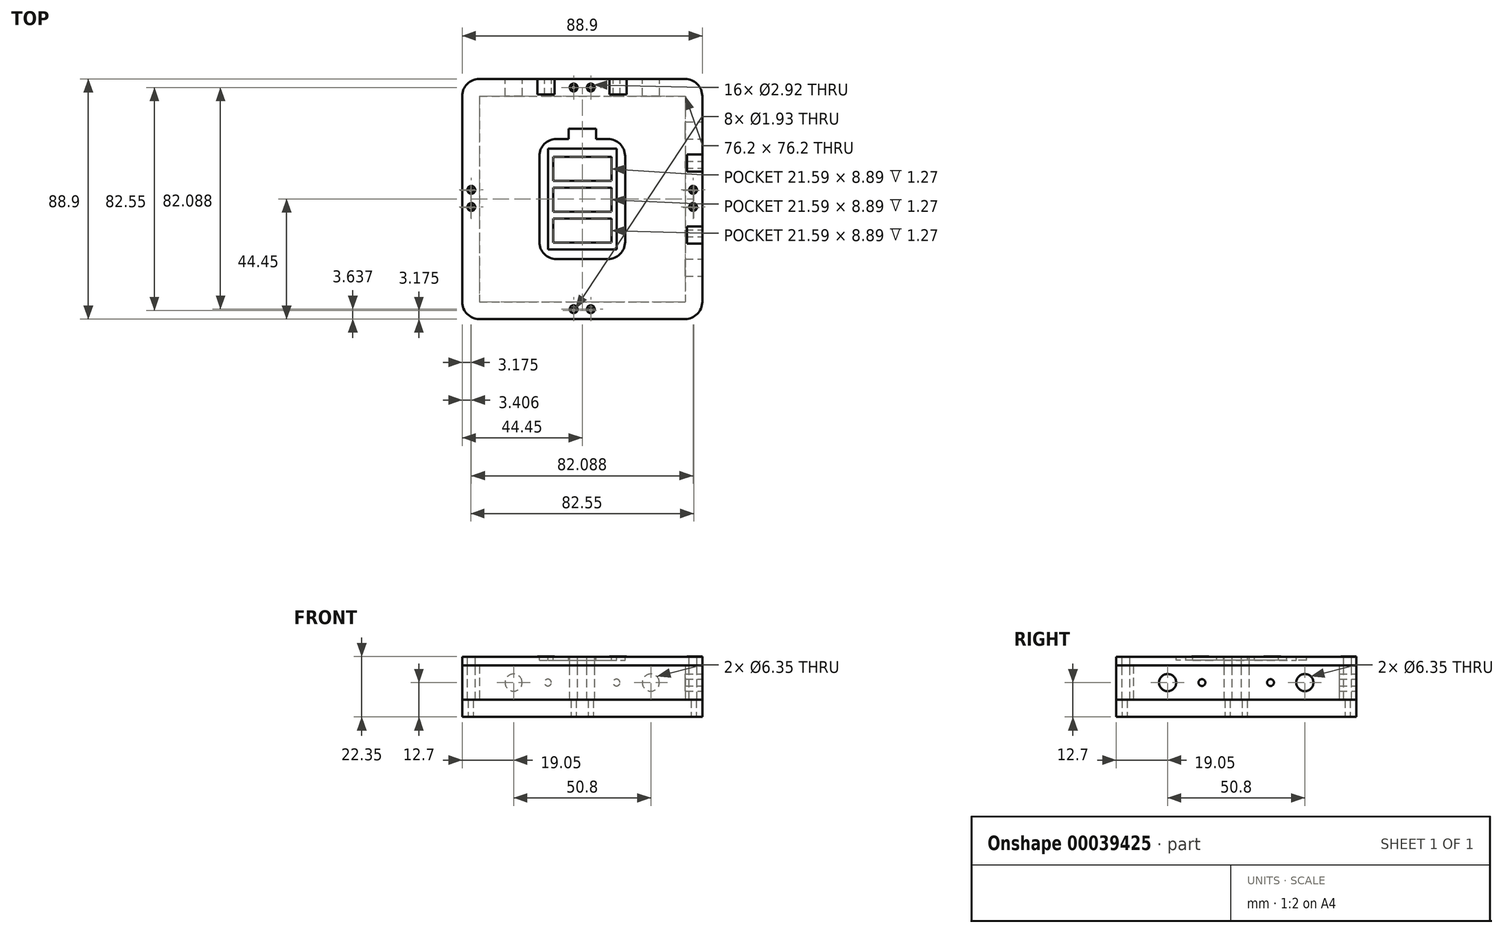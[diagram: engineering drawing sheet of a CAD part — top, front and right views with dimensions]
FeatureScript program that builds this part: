
annotation { "Feature Type Name" : "Feature", "Feature Type Description" : "" }
export const myFeature = defineFeature(function(context is Context, id is Id, definition is map)
    precondition{}
    {
        {
            var Q0;
            Q0=qCreatedBy(makeId("Top.planeOp"),FACE);
            var sketch = newSketch(context, id + "F0", { "sketchPlane" : qUnion([Q0])});
            skLineSegment(sketch, "E0.rect.bottom", {"start": v(-38.1, 44.45) * mm, "end": v(38.1, 44.45) * mm});
            skLineSegment(sketch, "E0.rect.top", {"start": v(-38.1, -44.45) * mm, "end": v(38.1, -44.45) * mm});
            skLineSegment(sketch, "E0.rect.left", {"start": v(-44.45, 38.1) * mm, "end": v(-44.45, -38.1) * mm});
            skLineSegment(sketch, "E0.rect.right", {"start": v(44.45, 38.1) * mm, "end": v(44.45, -38.1) * mm});
            skPoint(sketch, "E0.rect.middle", {"position": v(0, 0) * mm});
            skPoint(sketch, "E1.visualSharp", {"position": v(-44.45, 44.45) * mm});
            skArc(sketch, "E1.filletArc", {"start": v(-38.1, 44.45) * mm, "mid": v(-42.6, 42.6) * mm, "end": v(-44.45, 38.1) * mm});
            skPoint(sketch, "E2.visualSharp", {"position": v(44.45, 44.45) * mm});
            skArc(sketch, "E2.filletArc", {"start": v(44.45, 38.1) * mm, "mid": v(42.6, 42.6) * mm, "end": v(38.1, 44.45) * mm});
            skPoint(sketch, "E3.visualSharp", {"position": v(44.45, -44.45) * mm});
            skArc(sketch, "E3.filletArc", {"start": v(38.1, -44.45) * mm, "mid": v(42.6, -42.6) * mm, "end": v(44.45, -38.1) * mm});
            skPoint(sketch, "E4.visualSharp", {"position": v(-44.45, -44.45) * mm});
            skArc(sketch, "E4.filletArc", {"start": v(-44.45, -38.1) * mm, "mid": v(-42.6, -42.6) * mm, "end": v(-38.1, -44.45) * mm});
            skSolve(sketch);
        }
        {
            var Q0;
            Q0 = qSketchRegion(id + "F0", true);
            extrude(context, id + "F1", {"entities" : qUnion([Q0]), "depth" : 6.35 * mm});
        }
        {
            var Q0;
            Q0=makeQuery(id+"F1.opExtrude","CAP_FACE",FACE,{"disambiguationData":[OSD([sQuery(id+"F0.wireOp",EDGE,"E0.rect.bottom"),sQuery(id+"F0.wireOp",EDGE,"E0.rect.top"),sQuery(id+"F0.wireOp",EDGE,"E0.rect.left"),sQuery(id+"F0.wireOp",EDGE,"E0.rect.right"),sQuery(id+"F0.wireOp",EDGE,"E1.filletArc"),sQuery(id+"F0.wireOp",EDGE,"E2.filletArc"),sQuery(id+"F0.wireOp",EDGE,"E3.filletArc"),sQuery(id+"F0.wireOp",EDGE,"E4.filletArc")])],"isStart":false});
            var sketch = newSketch(context, id + "F2", { "sketchPlane" : qUnion([Q0])});
            skLineSegment(sketch, "E5.0", {"start": v(-38.1, 44.45) * mm, "end": v(38.1, 44.45) * mm});
            skArc(sketch, "E6.0", {"start": v(-38.1, 44.45) * mm, "mid": v(-42.6, 42.6) * mm, "end": v(-44.45, 38.1) * mm});
            skLineSegment(sketch, "E7.0", {"start": v(-44.45, 38.1) * mm, "end": v(-44.45, -38.1) * mm});
            skArc(sketch, "E8.0", {"start": v(-44.45, -38.1) * mm, "mid": v(-42.6, -42.6) * mm, "end": v(-38.1, -44.45) * mm});
            skLineSegment(sketch, "E9.0", {"start": v(-38.1, -44.45) * mm, "end": v(38.1, -44.45) * mm});
            skArc(sketch, "E10.0", {"start": v(38.1, -44.45) * mm, "mid": v(42.6, -42.6) * mm, "end": v(44.45, -38.1) * mm});
            skLineSegment(sketch, "E11.0", {"start": v(44.45, 38.1) * mm, "end": v(44.45, -38.1) * mm});
            skArc(sketch, "E12.0", {"start": v(44.45, 38.1) * mm, "mid": v(42.6, 42.6) * mm, "end": v(38.1, 44.45) * mm});
            skLineSegment(sketch, "E13.rect.bottom", {"start": v(-38.1, 38.1) * mm, "end": v(38.1, 38.1) * mm});
            skLineSegment(sketch, "E13.rect.top", {"start": v(-38.1, -38.1) * mm, "end": v(38.1, -38.1) * mm});
            skLineSegment(sketch, "E13.rect.left", {"start": v(-38.1, 38.1) * mm, "end": v(-38.1, -38.1) * mm});
            skLineSegment(sketch, "E13.rect.right", {"start": v(38.1, 38.1) * mm, "end": v(38.1, -38.1) * mm});
            skPoint(sketch, "E13.rect.middle", {"position": v(0, 0) * mm});
            skSolve(sketch);
        }
        {
            var Q0;
            Q0 = qSketchRegion(id + "F2", true);
            extrude(context, id + "F3", {"entities" : qUnion([Q0]), "depth" : 12.7 * mm});
        }
        {
            var Q0;
            Q0=makeQuery(id+"F3.opExtrude","SWEPT_FACE",FACE,{"disambiguationData":[OSD([sQuery(id+"F2.wireOp",EDGE,"E11.0")])]});
            var sketch = newSketch(context, id + "F4", { "sketchPlane" : qUnion([Q0])});
            skCircle(sketch, "E14", {"center": v(25.4, 12.7) * mm, "radius": 3.18 * mm});
            skPoint(sketch, "E14.centerSnap0", {"position": v(38.1, 12.7) * mm});
            skCircle(sketch, "E15", {"center": v(-25.4, 12.7) * mm, "radius": 3.18 * mm});
            skPoint(sketch, "E15.centerSnap0", {"position": v(-38.1, 12.7) * mm});
            skSolve(sketch);
        }
        {
            var Q0;
            Q0 = qSketchRegion(id + "F4", true);
            extrude(context, id + "F5", {"entities" : qUnion([Q0]), "operationType" : NewBodyOperationType.REMOVE, "oppositeDirection" : true, "depth" : 25.4 * mm});
        }
        {
            var Q0;
            Q0=makeQuery(id+"F3.opExtrude","SWEPT_FACE",FACE,{"disambiguationData":[OSD([sQuery(id+"F2.wireOp",EDGE,"E5.0")])]});
            var sketch = newSketch(context, id + "F6", { "sketchPlane" : qUnion([Q0])});
            skCircle(sketch, "E16", {"center": v(25.4, 12.7) * mm, "radius": 3.18 * mm});
            skPoint(sketch, "E16.centerSnap0", {"position": v(38.1, 12.7) * mm});
            skCircle(sketch, "E17", {"center": v(-25.4, 12.7) * mm, "radius": 3.18 * mm});
            skPoint(sketch, "E17.centerSnap0", {"position": v(-38.1, 12.7) * mm});
            skCircle(sketch, "E18", {"center": v(12.7, 12.7) * mm, "radius": 1.27 * mm});
            skCircle(sketch, "E19", {"center": v(-12.7, 12.7) * mm, "radius": 1.27 * mm});
            skSolve(sketch);
        }
        {
            var Q0;
            Q0 = qSketchRegion(id + "F6", true);
            extrude(context, id + "F7", {"entities" : qUnion([Q0]), "operationType" : NewBodyOperationType.REMOVE, "oppositeDirection" : true, "depth" : 25.4 * mm});
        }
        {
            var Q0;
            Q0=makeQuery(id+"F3.opExtrude","CAP_FACE",FACE,{"disambiguationData":[OSD([sQuery(id+"F2.wireOp",EDGE,"E5.0"),sQuery(id+"F2.wireOp",EDGE,"E6.0"),sQuery(id+"F2.wireOp",EDGE,"E7.0"),sQuery(id+"F2.wireOp",EDGE,"E8.0"),sQuery(id+"F2.wireOp",EDGE,"E9.0"),sQuery(id+"F2.wireOp",EDGE,"E10.0"),sQuery(id+"F2.wireOp",EDGE,"E11.0"),sQuery(id+"F2.wireOp",EDGE,"E12.0"),sQuery(id+"F2.wireOp",EDGE,"E13.rect.bottom"),sQuery(id+"F2.wireOp",EDGE,"E13.rect.top"),sQuery(id+"F2.wireOp",EDGE,"E13.rect.left"),sQuery(id+"F2.wireOp",EDGE,"E13.rect.right")])],"isStart":false});
            var sketch = newSketch(context, id + "F8", { "sketchPlane" : qUnion([Q0])});
            skArc(sketch, "E20.0", {"start": v(-38.1, 44.45) * mm, "mid": v(-42.6, 42.6) * mm, "end": v(-44.45, 38.1) * mm});
            skLineSegment(sketch, "E21.0", {"start": v(-38.1, 44.45) * mm, "end": v(38.1, 44.45) * mm});
            skArc(sketch, "E22.0", {"start": v(44.45, 38.1) * mm, "mid": v(42.6, 42.6) * mm, "end": v(38.1, 44.45) * mm});
            skLineSegment(sketch, "E23.0", {"start": v(44.45, 38.1) * mm, "end": v(44.45, -38.1) * mm});
            skArc(sketch, "E24.0", {"start": v(38.1, -44.45) * mm, "mid": v(42.6, -42.6) * mm, "end": v(44.45, -38.1) * mm});
            skLineSegment(sketch, "E25.0", {"start": v(-38.1, -44.45) * mm, "end": v(38.1, -44.45) * mm});
            skArc(sketch, "E26.0", {"start": v(-44.45, -38.1) * mm, "mid": v(-42.6, -42.6) * mm, "end": v(-38.1, -44.45) * mm});
            skLineSegment(sketch, "E27.0", {"start": v(-44.45, 38.1) * mm, "end": v(-44.45, -38.1) * mm});
            skSolve(sketch);
        }
        {
            var Q0;
            Q0 = qSketchRegion(id + "F8", true);
            extrude(context, id + "F9", {"entities" : qUnion([Q0]), "depth" : 3.17 * mm});
        }
        {
            var Q0;
            Q0=makeQuery(id+"F9.opExtrude","CAP_FACE",FACE,{"disambiguationData":[OSD([sQuery(id+"F8.wireOp",EDGE,"E20.0"),sQuery(id+"F8.wireOp",EDGE,"E21.0"),sQuery(id+"F8.wireOp",EDGE,"E22.0"),sQuery(id+"F8.wireOp",EDGE,"E23.0"),sQuery(id+"F8.wireOp",EDGE,"E24.0"),sQuery(id+"F8.wireOp",EDGE,"E25.0"),sQuery(id+"F8.wireOp",EDGE,"E26.0"),sQuery(id+"F8.wireOp",EDGE,"E27.0")])],"isStart":false});
            var sketch = newSketch(context, id + "F10", { "sketchPlane" : qUnion([Q0])});
            skCircle(sketch, "E28", {"center": v(-3.18, 41.28) * mm, "radius": 1.46 * mm});
            skCircle(sketch, "E29", {"center": v(3.17, 41.28) * mm, "radius": 1.46 * mm});
            skCircle(sketch, "E30.1.0", {"center": v(-41.04, -2.94) * mm, "radius": 1.46 * mm});
            skCircle(sketch, "E30.1.1", {"center": v(-41.04, 3.4) * mm, "radius": 1.46 * mm});
            skCircle(sketch, "E30.2.0", {"center": v(3.18, -40.81) * mm, "radius": 1.46 * mm});
            skCircle(sketch, "E30.2.1", {"center": v(-3.17, -40.81) * mm, "radius": 1.46 * mm});
            skCircle(sketch, "E30.3.0", {"center": v(41.04, 3.4) * mm, "radius": 1.46 * mm});
            skCircle(sketch, "E30.3.1", {"center": v(41.04, -2.94) * mm, "radius": 1.46 * mm});
            skPoint(sketch, "E30.center", {"position": v(0, 0.23) * mm});
            skSolve(sketch);
        }
        {
            var Q0;
            Q0 = qSketchRegion(id + "F10", true);
            extrude(context, id + "F11", {"entities" : qUnion([Q0]), "operationType" : NewBodyOperationType.REMOVE, "oppositeDirection" : true, "depth" : 15.88 * mm});
        }
        {
            var Q0;
            Q0=makeQuery(id+"F1.opExtrude","CAP_FACE",FACE,{"disambiguationData":[OSD([sQuery(id+"F0.wireOp",EDGE,"E0.rect.bottom"),sQuery(id+"F0.wireOp",EDGE,"E0.rect.top"),sQuery(id+"F0.wireOp",EDGE,"E0.rect.left"),sQuery(id+"F0.wireOp",EDGE,"E0.rect.right"),sQuery(id+"F0.wireOp",EDGE,"E1.filletArc"),sQuery(id+"F0.wireOp",EDGE,"E2.filletArc"),sQuery(id+"F0.wireOp",EDGE,"E3.filletArc"),sQuery(id+"F0.wireOp",EDGE,"E4.filletArc")])],"isStart":true});
            var sketch = newSketch(context, id + "F12", { "sketchPlane" : qUnion([Q0])});
            skCircle(sketch, "E31", {"center": v(3.18, -41.28) * mm, "radius": 0.97 * mm});
            skCircle(sketch, "E32", {"center": v(-3.17, -41.28) * mm, "radius": 0.97 * mm});
            skCircle(sketch, "E33.1.0", {"center": v(41.28, 3.18) * mm, "radius": 0.97 * mm});
            skCircle(sketch, "E33.1.1", {"center": v(41.28, -3.18) * mm, "radius": 0.97 * mm});
            skCircle(sketch, "E33.2.0", {"center": v(-3.17, 41.28) * mm, "radius": 0.97 * mm});
            skCircle(sketch, "E33.2.1", {"center": v(3.18, 41.28) * mm, "radius": 0.97 * mm});
            skCircle(sketch, "E33.3.0", {"center": v(-41.28, -3.17) * mm, "radius": 0.97 * mm});
            skCircle(sketch, "E33.3.1", {"center": v(-41.28, 3.18) * mm, "radius": 0.97 * mm});
            skPoint(sketch, "E33.center", {"position": v(0, 0) * mm});
            skSolve(sketch);
        }
        {
            var Q0;
            Q0 = qSketchRegion(id + "F12", true);
            extrude(context, id + "F13", {"entities" : qUnion([Q0]), "operationType" : NewBodyOperationType.REMOVE, "oppositeDirection" : true, "depth" : 6.35 * mm});
        }
        {
            var Q0;
            Q0=makeQuery(id+"F3.opExtrude","SWEPT_FACE",FACE,{"disambiguationData":[OSD([sQuery(id+"F2.wireOp",EDGE,"E11.0")])]});
            var sketch = newSketch(context, id + "F14", { "sketchPlane" : qUnion([Q0])});
            skCircle(sketch, "E34", {"center": v(-12.7, 12.7) * mm, "radius": 1.27 * mm});
            skPoint(sketch, "E34.centerSnap0", {"position": v(-38.1, 12.7) * mm});
            skCircle(sketch, "E35", {"center": v(12.7, 12.7) * mm, "radius": 1.27 * mm});
            skSolve(sketch);
        }
        {
            var Q0;
            Q0 = qSketchRegion(id + "F14", true);
            extrude(context, id + "F15", {"entities" : qUnion([Q0]), "operationType" : NewBodyOperationType.REMOVE, "oppositeDirection" : true, "depth" : 25.4 * mm});
        }
        {
            var Q0;
            Q0=makeQuery(id+"F9.opExtrude","CAP_FACE",FACE,{"disambiguationData":[OSD([sQuery(id+"F8.wireOp",EDGE,"E20.0"),sQuery(id+"F8.wireOp",EDGE,"E21.0"),sQuery(id+"F8.wireOp",EDGE,"E22.0"),sQuery(id+"F8.wireOp",EDGE,"E23.0"),sQuery(id+"F8.wireOp",EDGE,"E24.0"),sQuery(id+"F8.wireOp",EDGE,"E25.0"),sQuery(id+"F8.wireOp",EDGE,"E26.0"),sQuery(id+"F8.wireOp",EDGE,"E27.0")])],"isStart":false});
            var sketch = newSketch(context, id + "F16", { "sketchPlane" : qUnion([Q0])});
            skLineSegment(sketch, "E36.rect.bottom", {"start": v(-12.7, 18.64) * mm, "end": v(12.7, 18.64) * mm});
            skLineSegment(sketch, "E36.rect.top", {"start": v(-12.7, -18.64) * mm, "end": v(12.7, -18.64) * mm});
            skLineSegment(sketch, "E36.rect.left", {"start": v(-12.7, 18.64) * mm, "end": v(-12.7, -18.64) * mm});
            skLineSegment(sketch, "E36.rect.right", {"start": v(12.7, 18.64) * mm, "end": v(12.7, -18.64) * mm});
            skPoint(sketch, "E36.rect.middle", {"position": v(0, 0) * mm});
            skLineSegment(sketch, "E37.rect.bottom", {"start": v(-9.52, 22.25) * mm, "end": v(-5.08, 22.25) * mm});
            skLineSegment(sketch, "E37.rect.top", {"start": v(-9.53, -22.25) * mm, "end": v(9.52, -22.25) * mm});
            skLineSegment(sketch, "E37.rect.left", {"start": v(-15.87, 15.9) * mm, "end": v(-15.88, -15.9) * mm});
            skLineSegment(sketch, "E37.rect.right", {"start": v(15.88, 15.9) * mm, "end": v(15.87, -15.9) * mm});
            skPoint(sketch, "E38.visualSharp", {"position": v(-15.87, 22.25) * mm});
            skArc(sketch, "E38.filletArc", {"start": v(-9.52, 22.25) * mm, "mid": v(-14.02, 20.4) * mm, "end": v(-15.88, 15.9) * mm});
            skPoint(sketch, "E39.visualSharp", {"position": v(15.88, 22.25) * mm});
            skArc(sketch, "E39.filletArc", {"start": v(15.88, 15.9) * mm, "mid": v(14.02, 20.4) * mm, "end": v(9.53, 22.25) * mm});
            skPoint(sketch, "E40.visualSharp", {"position": v(15.87, -22.25) * mm});
            skArc(sketch, "E40.filletArc", {"start": v(9.52, -22.25) * mm, "mid": v(14.02, -20.4) * mm, "end": v(15.88, -15.9) * mm});
            skPoint(sketch, "E41.visualSharp", {"position": v(-15.88, -22.25) * mm});
            skArc(sketch, "E41.filletArc", {"start": v(-15.88, -15.9) * mm, "mid": v(-14.02, -20.4) * mm, "end": v(-9.53, -22.25) * mm});
            skLineSegment(sketch, "E42", {"start": v(-5.08, 22.25) * mm, "end": v(-5.08, 26.06) * mm});
            skLineSegment(sketch, "E43", {"start": v(-5.08, 26.06) * mm, "end": v(5.08, 26.06) * mm});
            skLineSegment(sketch, "E44", {"start": v(5.08, 26.06) * mm, "end": v(5.08, 22.25) * mm});
            skLineSegment(sketch, "E45.trimOffspring", {"start": v(5.08, 22.25) * mm, "end": v(9.53, 22.25) * mm});
            skLineSegment(sketch, "E46.rect.bottom", {"start": v(10.8, -16.1) * mm, "end": v(-10.8, -16.1) * mm});
            skLineSegment(sketch, "E46.rect.top", {"start": v(10.8, -7.21) * mm, "end": v(-10.8, -7.21) * mm});
            skLineSegment(sketch, "E46.rect.left", {"start": v(10.8, -16.1) * mm, "end": v(10.8, -7.21) * mm});
            skLineSegment(sketch, "E46.rect.right", {"start": v(-10.8, -16.1) * mm, "end": v(-10.8, -7.21) * mm});
            skPoint(sketch, "E46.rect.middle", {"position": v(0, -11.66) * mm});
            skLineSegment(sketch, "E47.rect.bottom", {"start": v(10.8, -4.67) * mm, "end": v(-10.8, -4.67) * mm});
            skLineSegment(sketch, "E47.rect.top", {"start": v(10.8, 4.22) * mm, "end": v(-10.8, 4.22) * mm});
            skLineSegment(sketch, "E47.rect.left", {"start": v(10.8, -4.67) * mm, "end": v(10.8, 4.22) * mm});
            skLineSegment(sketch, "E47.rect.right", {"start": v(-10.8, -4.67) * mm, "end": v(-10.8, 4.22) * mm});
            skPoint(sketch, "E47.rect.middle", {"position": v(0, -0.23) * mm});
            skLineSegment(sketch, "E48.rect.bottom", {"start": v(-10.8, 6.76) * mm, "end": v(10.8, 6.76) * mm});
            skLineSegment(sketch, "E48.rect.top", {"start": v(-10.8, 15.65) * mm, "end": v(10.8, 15.65) * mm});
            skLineSegment(sketch, "E48.rect.left", {"start": v(-10.8, 6.76) * mm, "end": v(-10.8, 15.65) * mm});
            skLineSegment(sketch, "E48.rect.right", {"start": v(10.8, 6.76) * mm, "end": v(10.8, 15.65) * mm});
            skPoint(sketch, "E48.rect.middle", {"position": v(0, 11.2) * mm});
            skSolve(sketch);
        }
        {
            var Q0;
            Q0 = qSketchRegion(id + "F16", true);
            var Q1;
            Q1=makeQuery(id+"F16.imprint","IMPRINT",FACE,{"disambiguationData":[TD([[makeQuery(id+"F16.imprint","IMPRINT",EDGE,{"derivedFrom":sQuery(id+"F16.wireOp",EDGE,"E48.rect.bottom")}),1.0]])]});
            var Q2;
            Q2=makeQuery(id+"F16.imprint","IMPRINT",FACE,{"disambiguationData":[TD([[makeQuery(id+"F16.imprint","IMPRINT",EDGE,{"derivedFrom":sQuery(id+"F16.wireOp",EDGE,"E47.rect.bottom")}),-1.0]])]});
            var Q3;
            Q3=makeQuery(id+"F16.imprint","IMPRINT",FACE,{"disambiguationData":[TD([[makeQuery(id+"F16.imprint","IMPRINT",EDGE,{"derivedFrom":sQuery(id+"F16.wireOp",EDGE,"E46.rect.bottom")}),-1.0]])]});
            extrude(context, id + "F17", {"entities" : qUnion([Q0, Q1, Q2, Q3]), "operationType" : NewBodyOperationType.REMOVE, "oppositeDirection" : true, "depth" : 1.27 * mm});
        }
        {
            var Q0;
            Q0=makeQuery(id+"F3.opExtrude","SWEPT_FACE",FACE,{"disambiguationData":[OSD([sQuery(id+"F2.wireOp",EDGE,"E11.0")])]});
            var sketch = newSketch(context, id + "F18", { "sketchPlane" : qUnion([Q0])});
            skCircle(sketch, "E49.0", {"center": v(25.4, 12.7) * mm, "radius": 3.18 * mm});
            skCircle(sketch, "E50.0", {"center": v(-25.4, 12.7) * mm, "radius": 3.18 * mm});
            skCircle(sketch, "E51.0", {"center": v(-12.7, 12.7) * mm, "radius": 1.27 * mm});
            skCircle(sketch, "E52.0", {"center": v(12.7, 12.7) * mm, "radius": 1.27 * mm});
            skSolve(sketch);
        }
        {
            var Q0;
            Q0 = qSketchRegion(id + "F18", true);
            extrude(context, id + "F19", {"entities" : qUnion([Q0]), "oppositeDirection" : true, "depth" : 6.35 * mm});
        }
        {
            var Q0;
            Q0=makeQuery(id+"F3.opExtrude","SWEPT_FACE",FACE,{"disambiguationData":[OSD([sQuery(id+"F2.wireOp",EDGE,"E5.0")])]});
            var sketch = newSketch(context, id + "F20", { "sketchPlane" : qUnion([Q0])});
            skCircle(sketch, "E53.0", {"center": v(25.4, 12.7) * mm, "radius": 3.18 * mm});
            skCircle(sketch, "E54.0", {"center": v(12.7, 12.7) * mm, "radius": 1.27 * mm});
            skCircle(sketch, "E55.0", {"center": v(-12.7, 12.7) * mm, "radius": 1.27 * mm});
            skCircle(sketch, "E56.0", {"center": v(-25.4, 12.7) * mm, "radius": 3.18 * mm});
            skSolve(sketch);
        }
        {
            var Q0;
            Q0 = qSketchRegion(id + "F20", true);
            extrude(context, id + "F21", {"entities" : qUnion([Q0]), "oppositeDirection" : true, "depth" : 6.35 * mm});
        }
        {
            var Q0;
            {var subQ0=sQuery(id+"F8.wireOp",EDGE,"E20.0");var subQ1=sQuery(id+"F8.wireOp",EDGE,"E21.0");var subQ2=sQuery(id+"F8.wireOp",EDGE,"E22.0");var subQ3=sQuery(id+"F8.wireOp",EDGE,"E23.0");var subQ4=sQuery(id+"F8.wireOp",EDGE,"E24.0");var subQ5=sQuery(id+"F8.wireOp",EDGE,"E25.0");var subQ6=sQuery(id+"F8.wireOp",EDGE,"E26.0");var subQ7=sQuery(id+"F8.wireOp",EDGE,"E27.0");Q0=makeQuery(id+"F17.boolean.opBoolean","SPLIT",FACE,{"disambiguationData":[TD([makeQuery(id+"F9.opExtrude","SWEPT_FACE",FACE,{"disambiguationData":[OSD([subQ0])]})])],"derivedFrom":makeQuery(id+"F9.opExtrude","CAP_FACE",FACE,{"disambiguationData":[OSD([subQ0,subQ1,subQ2,subQ3,subQ4,subQ5,subQ6,subQ7])],"isStart":false})});}
            var sketch = newSketch(context, id + "F22", { "sketchPlane" : qUnion([Q0])});
            skLineSegment(sketch, "E57.bottom", {"start": v(44.45, 10.16) * mm, "end": v(38.74, 10.16) * mm});
            skLineSegment(sketch, "E57.top", {"start": v(44.45, 16.51) * mm, "end": v(38.74, 16.51) * mm});
            skLineSegment(sketch, "E57.left", {"start": v(44.45, 10.16) * mm, "end": v(44.45, 16.51) * mm});
            skLineSegment(sketch, "E57.right", {"start": v(38.74, 10.16) * mm, "end": v(38.74, 16.51) * mm});
            skLineSegment(sketch, "E58.bottom", {"start": v(44.45, -10.16) * mm, "end": v(38.74, -10.16) * mm});
            skLineSegment(sketch, "E58.top", {"start": v(44.45, -16.51) * mm, "end": v(38.74, -16.51) * mm});
            skLineSegment(sketch, "E58.left", {"start": v(44.45, -10.16) * mm, "end": v(44.45, -16.5) * mm});
            skLineSegment(sketch, "E58.right", {"start": v(38.74, -10.16) * mm, "end": v(38.74, -16.5) * mm});
            skPoint(sketch, "E59.center", {"position": v(0, 1.27) * mm});
            skLineSegment(sketch, "E60.1.0", {"start": v(-16.51, 44.45) * mm, "end": v(-16.51, 38.74) * mm});
            skLineSegment(sketch, "E60.1.1", {"start": v(-10.16, 44.45) * mm, "end": v(-16.51, 44.45) * mm});
            skLineSegment(sketch, "E60.1.2", {"start": v(-10.16, 38.74) * mm, "end": v(-16.51, 38.74) * mm});
            skLineSegment(sketch, "E60.1.3", {"start": v(-10.16, 44.45) * mm, "end": v(-10.16, 38.74) * mm});
            skLineSegment(sketch, "E60.1.4", {"start": v(10.16, 44.45) * mm, "end": v(10.16, 38.74) * mm});
            skLineSegment(sketch, "E60.1.5", {"start": v(10.16, 44.45) * mm, "end": v(16.51, 44.45) * mm});
            skLineSegment(sketch, "E60.1.6", {"start": v(10.16, 38.74) * mm, "end": v(16.5, 38.74) * mm});
            skLineSegment(sketch, "E60.1.7", {"start": v(16.51, 44.45) * mm, "end": v(16.51, 38.74) * mm});
            skPoint(sketch, "E60.center", {"position": v(0, 0) * mm});
            skLineSegment(sketch, "E60.anchor1", {"start": v(0, 0) * mm, "end": v(38.74, 16.51) * mm, "construction": true});
            skLineSegment(sketch, "E60.anchor2", {"start": v(0, 0) * mm, "end": v(-16.51, 38.74) * mm, "construction": true});
            skSolve(sketch);
        }
        {
            var Q0;
            Q0 = qSketchRegion(id + "F22", true);
            extrude(context, id + "F23", {"entities" : qUnion([Q0]), "depth" : 0.13 * mm});
        }
    });
